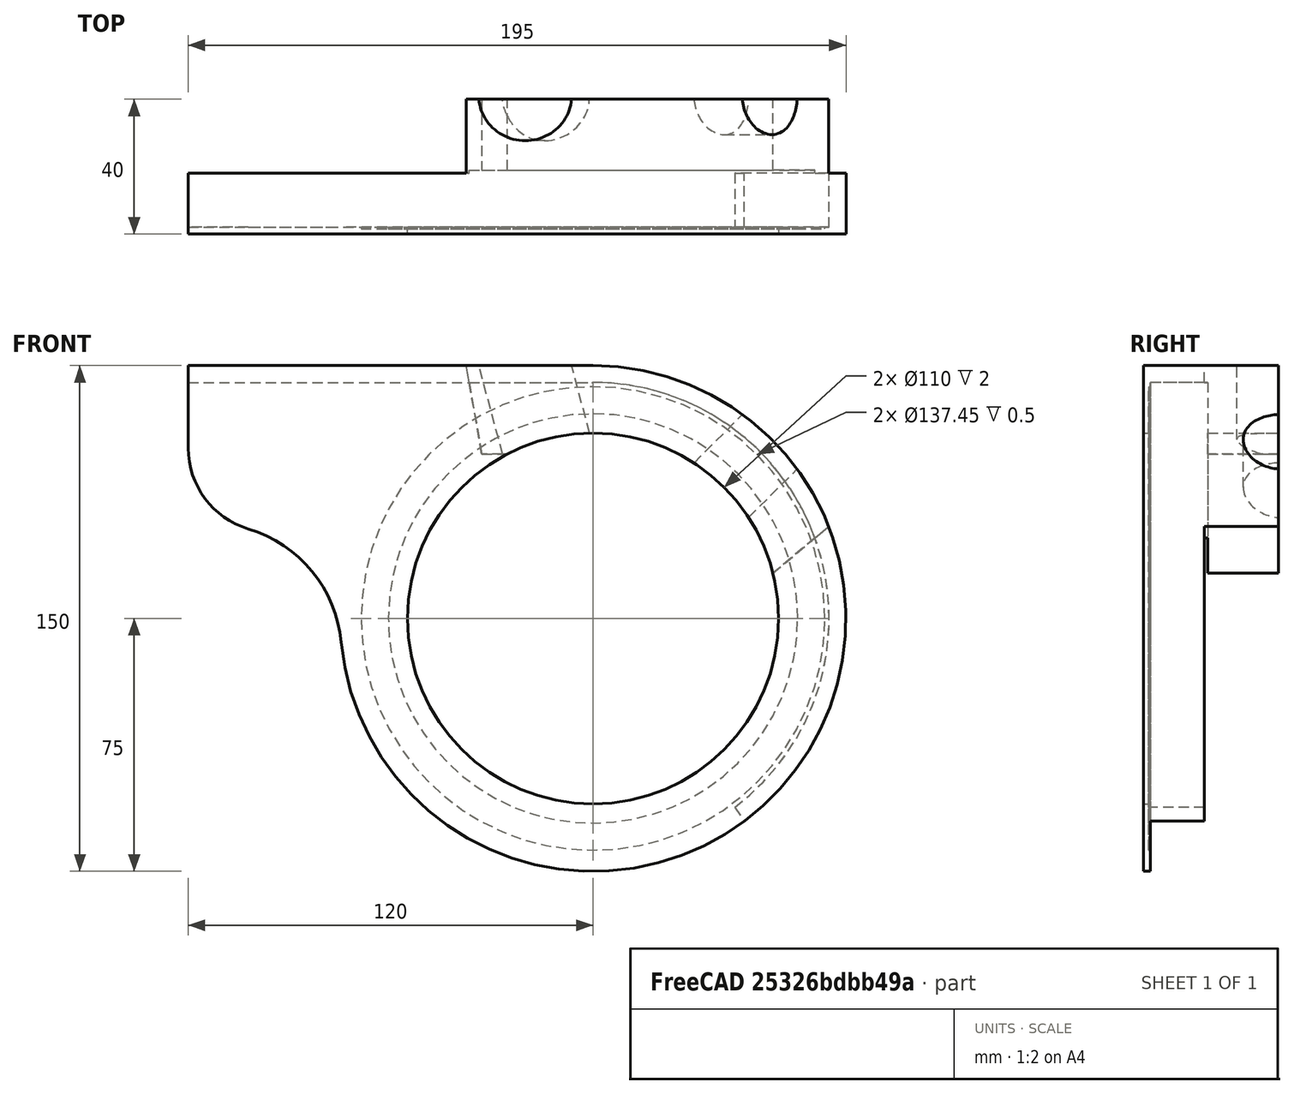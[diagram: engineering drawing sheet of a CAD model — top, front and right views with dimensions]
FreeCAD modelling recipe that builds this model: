
FCSTD DOCUMENT  (FreeCAD 0.19R)
Label: BottomWhiteBike2
License: All rights reserved
LicenseURL: http://en.wikipedia.org/wiki/All_rights_reserved
objects: Sketcher::SketchObject×4, PartDesign::Pocket×3, Part::Cylinder×2, PartDesign::Pad×1, Part::MultiFuse×1, PartDesign::Body×1, Part::Cut×1, Mesh::Feature×1
note: 17 computed .brp shape members not serialized (recipe doc carries the construction recipe); baked Part::Feature solids carry a one-line shape summary decoded from their .brp

FEATURE [Sketcher::SketchObject] Sketch
  FullyConstrained = false
  MapMode = 5
  Placement = pos=(0,0,0) rot=(1,0,0;1.5708rad)
  Support = -> [XZ_Plane]
  sketch-geometry (11):
    g0: LineSegment StartX=0 StartY=0 StartZ=0 EndX=112.706 EndY=65.0706 EndZ=0
    g1: LineSegment StartX=0 StartY=0 StartZ=0 EndX=7.3e-15 EndY=119.149 EndZ=0
    g2: LineSegment StartX=2.14e-14 StartY=70 StartZ=0 EndX=-199.884 EndY=70 EndZ=0
    g3: Circle CenterX=0 CenterY=0 CenterZ=0 NormalX=0 NormalY=0 NormalZ=1 AngleXU=0 Radius=45
    g4: ArcOfCircle CenterX=0 CenterY=0 CenterZ=0 NormalX=0 NormalY=0 NormalZ=1 AngleXU=0 Radius=70 StartAngle=3.5224 EndAngle=7.85398
    g5: LineSegment StartX=-120 StartY=75 StartZ=0 EndX=2.84e-14 EndY=75 EndZ=0
    g6: ArcOfCircle CenterX=0 CenterY=0 CenterZ=0 NormalX=0 NormalY=0 NormalZ=1 AngleXU=0 Radius=75 StartAngle=3.23571 EndAngle=7.85398
    g7: LineSegment StartX=-120 StartY=75 StartZ=0 EndX=-120 EndY=50.5061 EndZ=0
    g8: ArcOfCircle CenterX=-95 CenterY=50.5061 CenterZ=0 NormalX=0 NormalY=0 NormalZ=1 AngleXU=0 Radius=25 StartAngle=3.14159 EndAngle=4.4201
    g9: Circle CenterX=0 CenterY=0 CenterZ=0 NormalX=0 NormalY=0 NormalZ=1 AngleXU=0 Radius=55
    g10: ArcOfCircle CenterX=-113.419 CenterY=-10.7061 CenterZ=0 NormalX=0 NormalY=0 NormalZ=1 AngleXU=0 Radius=38.9235 StartAngle=0.0941155 EndAngle=1.27851
  constraints (25):
    c: Coincident(g0,g-1)
    c: Coincident(g1,g-1)
    c: Angle(g1) = 1.5708
    c: Angle(g0,g1) = 1.0472
    c: PointOnObject(g2,g1)
    c: Angle(g2) = 3.14159
    c: DistanceY(g2) = 70
    c: Coincident(g3,g-1)
    c: Coincident(g4,g-1)
    c: Diameter(g3) = 90
    c: Coincident(g4,g2)
    c: PointOnObject(g5,g1)
    c: Horizontal(g5)
    c: Coincident(g6,g-1)
    c: Coincident(g6,g5)
    c: Coincident(g5,g7)
    c: Vertical(g7)
    c: Tangent(g8,g7) = -1.5708
    c: Diameter(g6) = 150
    c: Distance(g5) = 120
    c: Diameter(g8) = 50
    c: Coincident(g9,g6)
    c: Diameter(g9) = 110
    c: Tangent(g10,g6) = 1.5708
    c: Tangent(g10,g8) = 1.5708
FEATURE [PartDesign::Pad] Pad
  Direction = (1,1,1)
  Length = 40
  Length2 = 100
  Placement = pos=(0,0,0) rot=(1,0,0;1.5708rad)
  Profile = -> Sketch
  Type = 0
FEATURE [Sketcher::SketchObject] Sketch001
  FullyConstrained = false
  MapMode = 5
  Placement = pos=(0,0,0) rot=(-1,0,0;1.5708rad)
  Support = -> [Pad]
  sketch-geometry (10):
    g0: GeomPoint X=0 Y=0 Z=0
    g1: LineSegment StartX=0 StartY=0 StartZ=0 EndX=122.795 EndY=-103.038 EndZ=0
    g2: LineSegment StartX=52.0812 StartY=-12.3715 StartZ=0 EndX=85.5524 EndY=-40.4572 EndZ=0
    g3: ArcOfCircle CenterX=0 CenterY=0 CenterZ=0 NormalX=0 NormalY=0 NormalZ=1 AngleXU=0 Radius=94.6362 StartAngle=5.84146 EndAngle=9.42478
    g4: LineSegment StartX=-211.759 StartY=-108.832 StartZ=0 EndX=-94.6362 EndY=2.84e-14 EndZ=0
    g5: LineSegment StartX=52.0812 StartY=-12.3715 StartZ=0 EndX=21.2274 EndY=-49.1417 EndZ=0
    g6: LineSegment StartX=21.2274 StartY=-49.1417 StartZ=0 EndX=-32.9654 EndY=-48.7455 EndZ=0
    g7: LineSegment StartX=-32.9654 StartY=-48.7455 StartZ=0 EndX=-43.5602 EndY=-108.832 EndZ=0
    g8: LineSegment StartX=-43.5602 StartY=-108.832 StartZ=0 EndX=-211.759 EndY=-108.832 EndZ=0
    g9: LineSegment StartX=0 StartY=0 StartZ=0 EndX=-35.8436 EndY=-203.279 EndZ=0
  constraints (19):
    c: Coincident(g1,g-1)
    c: Angle(g1,g-2) = 2.26893
    c: Coincident(g3,g-1)
    c: Coincident(g3,g2)
    c: PointOnObject(g3,g-1)
    c: Coincident(g4,g3)
    c: Coincident(g2,g5)
    c: Coincident(g6,g7)
    c: Coincident(g7,g8)
    c: Horizontal(g8)
    c: Coincident(g4,g8)
    c: Symmetric(g2,g5,g1)
    c: Distance(g2,g1) = 24
    c: Coincident(g5,g6)
    c: Parallel(g2,g1)
    c: Coincident(g9,g3)
    c: Angle(g9,g1) = 1.0472
    c: Parallel(g9,g7)
    c: Distance(g7,g9) = 24
FEATURE [PartDesign::Pocket] Pocket  label="FirstPocket-trim"
  BaseFeature = -> Pad
  Length = 22
  Length2 = 100
  Placement = pos=(0,0,0) rot=(1,0,0;1.5708rad)
  Profile = -> Sketch001
  Type = 0
FEATURE [Sketcher::SketchObject] Sketch003
  FullyConstrained = false
  MapMode = 5
  Placement = pos=(0,-22,2.44e-14) rot=(-1,0,0;1.5708rad)
  Support = -> [Pocket]
  sketch-geometry (5):
    g0: ArcOfCircle CenterX=0 CenterY=0 CenterZ=0 NormalX=0 NormalY=0 NormalZ=1 AngleXU=0 Radius=70 StartAngle=4.71239 EndAngle=7.21016
    g1: LineSegment StartX=42.0181 StartY=55.9864 StartZ=0 EndX=62.2266 EndY=86.1683 EndZ=0
    g2: LineSegment StartX=62.2266 StartY=86.1683 StartZ=0 EndX=-170.809 EndY=86.1683 EndZ=0
    g3: LineSegment StartX=-170.809 StartY=86.1683 StartZ=0 EndX=-170.809 EndY=-70 EndZ=0
    g4: LineSegment StartX=-170.809 StartY=-70 StartZ=0 EndX=0 EndY=-70 EndZ=0
  constraints (11):
    c: Coincident(g0,g-1)
    c: PointOnObject(g0,g-2)
    c: Diameter(g0) = 140
    c: Coincident(g1,g0)
    c: Coincident(g1,g2)
    c: Horizontal(g2)
    c: Coincident(g2,g3)
    c: Vertical(g3)
    c: Coincident(g3,g4)
    c: Coincident(g4,g0)
    c: Horizontal(g4)
FEATURE [PartDesign::Pocket] Pocket001  label="2ndPocket-thk"
  BaseFeature = -> Pocket
  Length = 16
  Length2 = 1
  Placement = pos=(0,0,0) rot=(1,0,0;1.5708rad)
  Profile = -> Sketch003
  Type = 4
FEATURE [Part::Cylinder] Cylinder  label="DT"
  Angle = 360
  AttacherType = Attacher::AttachEngine3D
  Height = 150
  Placement = pos=(0,1,0) rot=(0,1,0;0.785398rad)
  Radius = 11.5
FEATURE [Part::Cylinder] Cylinder001  label="ST"
  Angle = 360
  AttacherType = Attacher::AttachEngine3D
  Height = 150
  Placement = pos=(0,1,0) rot=(0,1,0;-0.261799rad)
  Radius = 13.3
FEATURE [Part::MultiFuse] Fusion
  Shapes = -> [Cylinder,Cylinder001]
FEATURE [Sketcher::SketchObject] Sketch004
  FullyConstrained = false
  MapMode = 5
  Placement = pos=(1e-16,-38,4.23e-14) rot=(0,0.707107,0.707107;3.14159rad)
  sketch-geometry (2):
    g0: Circle CenterX=0 CenterY=0 CenterZ=0 NormalX=0 NormalY=0 NormalZ=1 AngleXU=0 Radius=68.7241
    g1: Circle CenterX=0 CenterY=0 CenterZ=0 NormalX=0 NormalY=0 NormalZ=1 AngleXU=0 Radius=60.6833
  constraints (2):
    c: Coincident(g0,g-1)
    c: Coincident(g1,g0)
FEATURE [PartDesign::Pocket] Pocket002
  BaseFeature = -> Pocket001
  Length = 0.5
  Length2 = 100
  Placement = pos=(0,0,0) rot=(1,0,0;1.5708rad)
  Profile = -> Sketch004
  Type = 0
FEATURE [PartDesign::Body] Body
  Group = -> [Sketch,Pad,Sketch001,Pocket,Sketch003,Pocket001,Sketch004,Pocket002]
  Origin = -> Origin
  Tip = -> Pocket002
FEATURE [Part::Cut] Cut
  Base = -> Pocket002
  Tool = -> Fusion
FEATURE [Mesh::Feature] Mesh  label="Cut (Meshed)"
